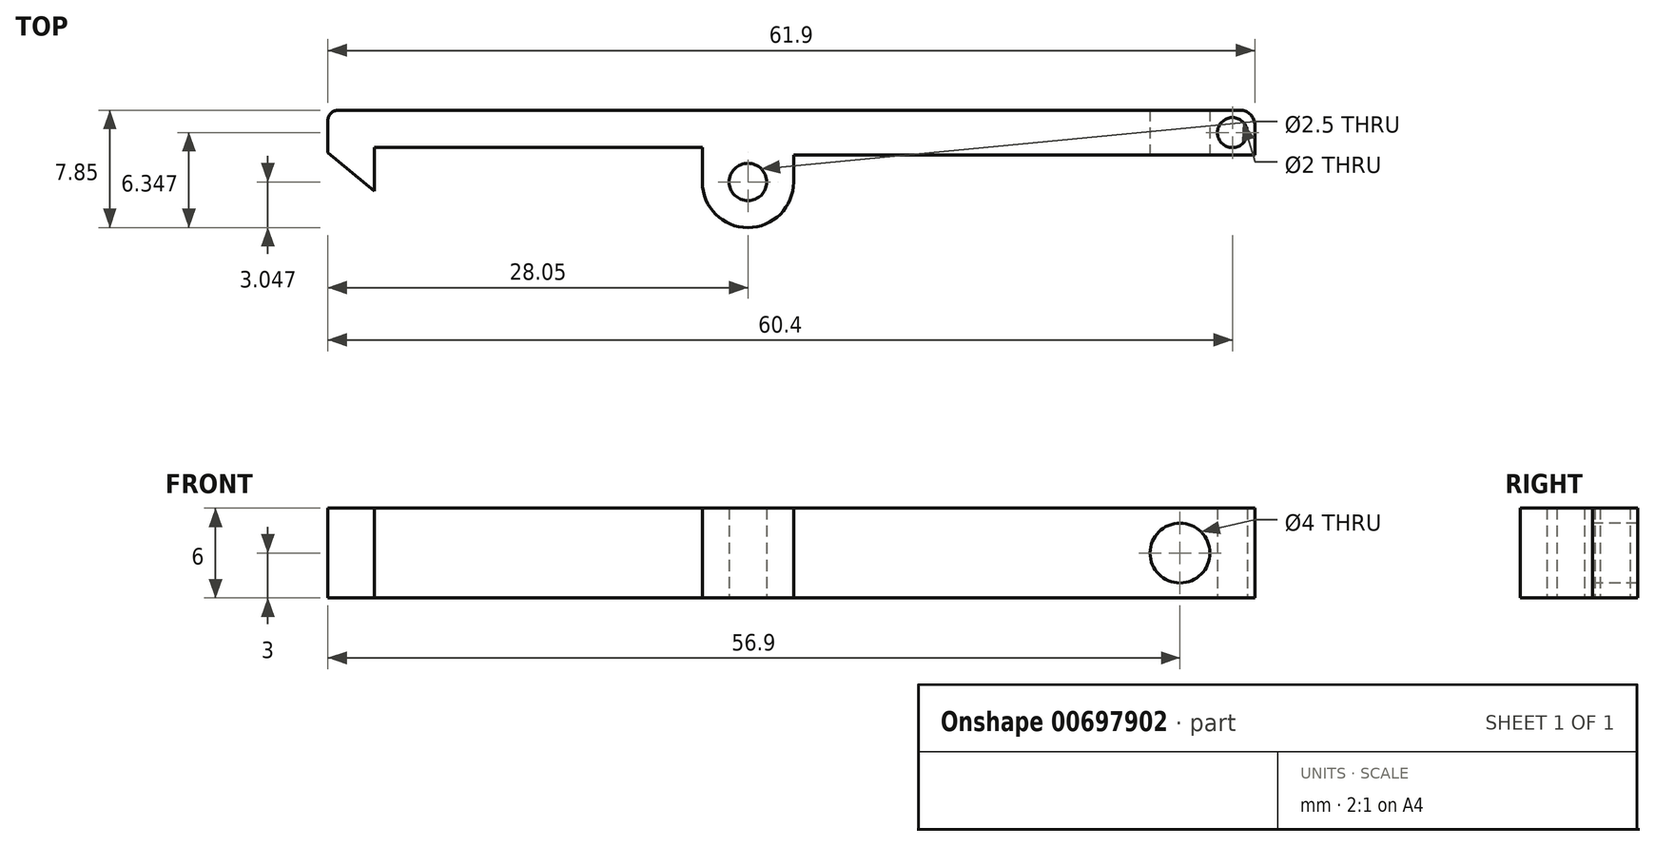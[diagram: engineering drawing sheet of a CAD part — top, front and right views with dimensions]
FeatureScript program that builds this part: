
annotation { "Feature Type Name" : "Feature", "Feature Type Description" : "" }
export const myFeature = defineFeature(function(context is Context, id is Id, definition is map)
    precondition{}
    {
        {
            var Q0;
            Q0=qCreatedBy(makeId("Top.planeOp"),FACE);
            var sketch = newSketch(context, id + "F0", { "sketchPlane" : qUnion([Q0])});
            skLineSegment(sketch, "E0.top", {"start": v(0.7, 2.84) * mm, "end": v(60.9, 2.84) * mm});
            skLineSegment(sketch, "E0.left", {"start": v(0, 0) * mm, "end": v(0, 2.14) * mm});
            skLineSegment(sketch, "E0.right", {"start": v(61.9, -0.16) * mm, "end": v(61.9, 1.84) * mm});
            skLineSegment(sketch, "E1", {"start": v(3.1, 0.34) * mm, "end": v(3.1, -2.56) * mm});
            skLineSegment(sketch, "E2", {"start": v(3.1, -2.56) * mm, "end": v(0, 0) * mm});
            skLineSegment(sketch, "E3.left", {"start": v(25, 0.34) * mm, "end": v(25, -1.96) * mm});
            skLineSegment(sketch, "E3.right", {"start": v(31.1, -0.16) * mm, "end": v(31.1, -1.96) * mm});
            skArc(sketch, "E4", {"start": v(25, -1.96) * mm, "mid": v(28.05, -5.01) * mm, "end": v(31.1, -1.96) * mm});
            skCircle(sketch, "E5", {"center": v(28.05, -1.96) * mm, "radius": 1.25 * mm});
            skLineSegment(sketch, "E6.trimOffspring", {"start": v(31.1, -0.16) * mm, "end": v(61.9, -0.16) * mm});
            skPoint(sketch, "E7.centerSnap0", {"position": v(46.5, -0.16) * mm});
            skCircle(sketch, "E8", {"center": v(60.4, 1.34) * mm, "radius": 1 * mm});
            skLineSegment(sketch, "E9", {"start": v(3.1, 0.34) * mm, "end": v(25, 0.34) * mm});
            skPoint(sketch, "E10.visualSharp", {"position": v(0, 2.84) * mm});
            skArc(sketch, "E10.filletArc", {"start": v(0.7, 2.84) * mm, "mid": v(0.2, 2.63) * mm, "end": v(0, 2.14) * mm});
            skPoint(sketch, "E11.visualSharp", {"position": v(61.9, 2.84) * mm});
            skArc(sketch, "E11.filletArc", {"start": v(61.9, 1.84) * mm, "mid": v(61.6, 2.54) * mm, "end": v(60.9, 2.84) * mm});
            skPoint(sketch, "E12.end.orphan", {"position": v(3.1, 0) * mm});
            skPoint(sketch, "E13.orphan", {"position": v(25, 0) * mm});
            skSolve(sketch);
        }
        {
            var Q0;
            Q0=makeQuery(id+"F0.imprint","IMPRINT",FACE,{"disambiguationData":[TD([[makeQuery(id+"F0.imprint","IMPRINT",EDGE,{"derivedFrom":sQuery(id+"F0.wireOp",EDGE,"E0.top")}),-1.0]])]});
            extrude(context, id + "F1", {"entities" : qUnion([Q0]), "depth" : 6 * mm, "offsetDistance" : 25 * mm});
        }
        {
            var Q0;
            Q0=makeQuery(id+"F1.opExtrude","SWEPT_FACE",FACE,{"disambiguationData":[OSD([sQuery(id+"F0.wireOp",EDGE,"E6.trimOffspring")])]});
            var sketch = newSketch(context, id + "F2", { "sketchPlane" : qUnion([Q0])});
            skCircle(sketch, "E14", {"center": v(56.9, 3) * mm, "radius": 2 * mm});
            skSolve(sketch);
        }
        {
            var Q0;
            Q0 = qSketchRegion(id + "F2", true);
            extrude(context, id + "F3", {"entities" : qUnion([Q0]), "operationType" : NewBodyOperationType.REMOVE, "oppositeDirection" : true, "depth" : 25 * mm, "offsetDistance" : 25 * mm});
        }
    });
